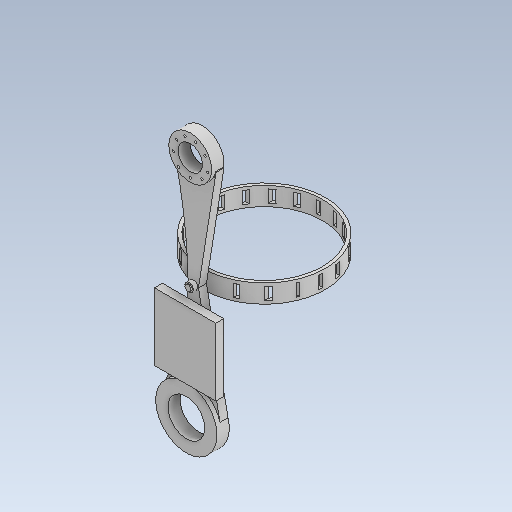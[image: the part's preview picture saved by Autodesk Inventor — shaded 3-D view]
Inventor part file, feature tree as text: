
AUTODESK INVENTOR PART (.ipt)
format: ipt  version: 2021 (Build 250183000, 183)  size: 305,664 bytes
history: native  units: mm
features: sketch x19, other x4, plane x1
ambient origin geometry x8: Origin, YZ Plane, XZ Plane, XY Plane, X Axis, Y Axis, Z Axis, Center Point
bodies: Solid1 (feature_tree), Solid2 (feature_tree)
feature tree (24):
  other  "Thigh Support.ipt"
  other  "Solid1::Thigh Support.ipt"
  other  "Solid2::Thigh Support.ipt"
  other  "TaggingFeature1"
  sketch  "Sketch1"  dims[d0=10.0mm]
  sketch  "Sketch2"
  sketch  "Sketch3"
  sketch  "Sketch4"
  sketch  "Sketch5"
  sketch  "Sketch6"
  sketch  "Sketch7"
  sketch  "Sketch8"
  sketch  "Sketch9"
  sketch  "Sketch10"
  sketch  "Sketch11"
  sketch  "Sketch12"
  sketch  "Sketch13"
  sketch  "Sketch14"
  sketch  "Sketch15"
  sketch  "Sketch16"
  sketch  "Sketch17"
  sketch  "Sketch18"
  sketch  "Sketch19"
  plane  "Work Plane1"
